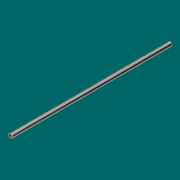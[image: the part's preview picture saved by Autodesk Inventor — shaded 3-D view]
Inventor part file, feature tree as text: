
AUTODESK INVENTOR PART (.ipt)
format: ipt  version: 2017 (Build 210142000, 142)  size: 68,096 bytes
history: native  units: in
note: dims shown in document units (in); Inventor stores cm internally (conversion verified against a paired STEP export)
features: extrude x1, sketch x1
ambient origin geometry x8: Origin, YZ Plane, XZ Plane, XY Plane, X Axis, Y Axis, Z Axis, Center Point
bodies: Solid1 (feature_tree)
feature tree (2):
  extrude  "Extrusion1"  Depth=84.0in TaperAngle=0.0deg
  sketch  "Sketch1"  dims[d0=2.25in d1=84.0in d2=0.0in]
